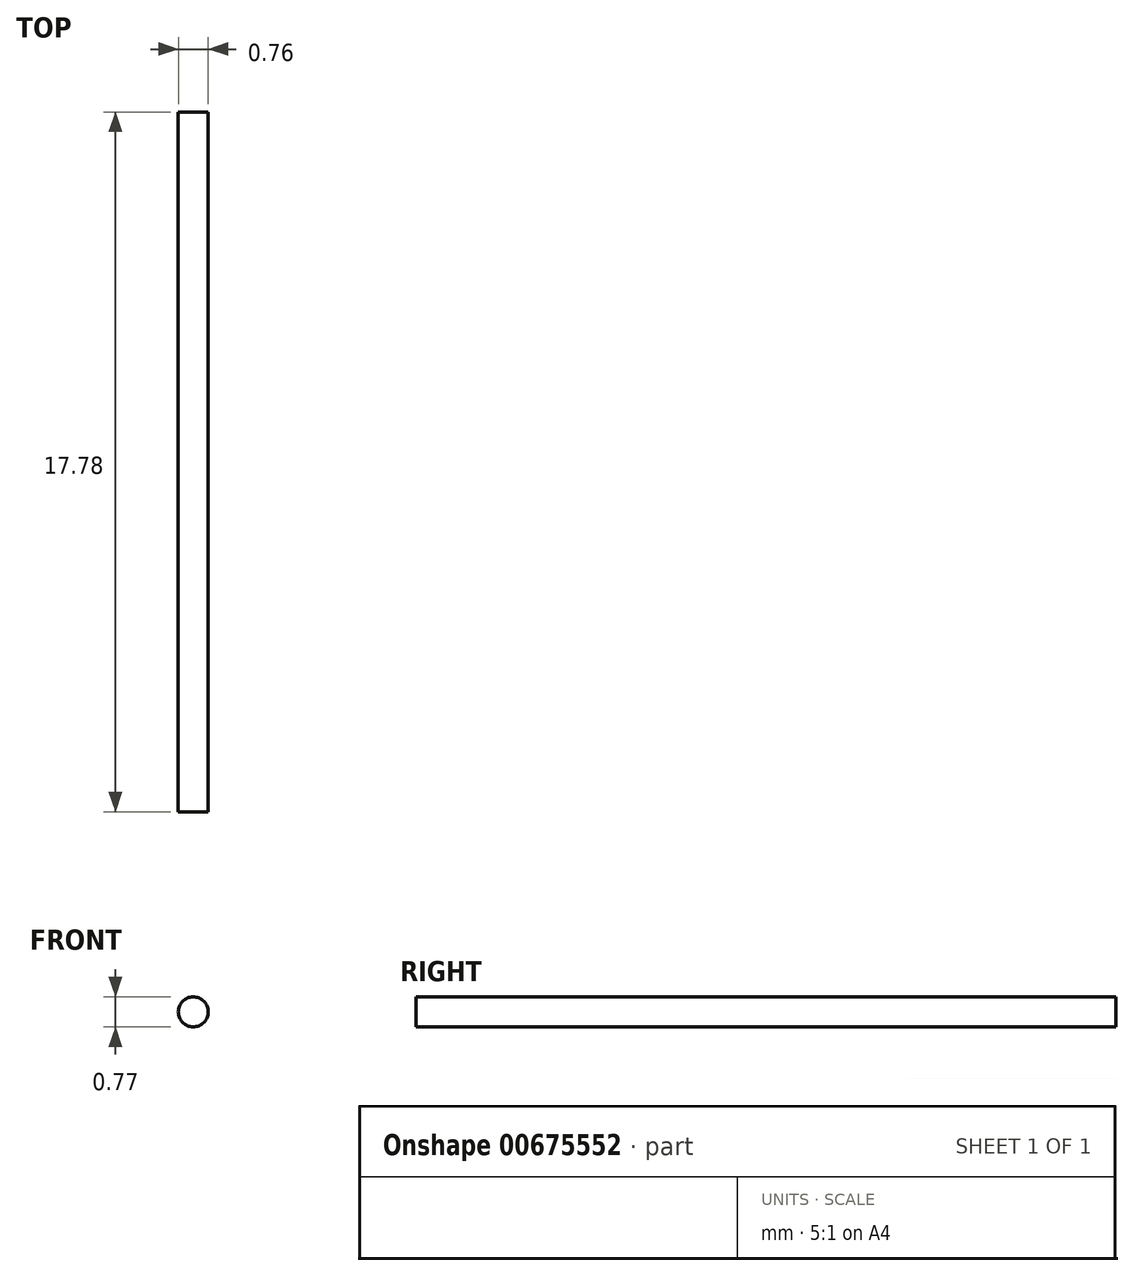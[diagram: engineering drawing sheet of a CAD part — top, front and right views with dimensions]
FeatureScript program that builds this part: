
annotation { "Feature Type Name" : "Feature", "Feature Type Description" : "" }
export const myFeature = defineFeature(function(context is Context, id is Id, definition is map)
    precondition{}
    {
        {
            var Q0;
            Q0=qCreatedBy(makeId("Front.planeOp"),FACE);
            var sketch = newSketch(context, id + "F0", { "sketchPlane" : qUnion([Q0])});
            skCircle(sketch, "E0", {"center": v(-44.96, 25.03) * mm, "radius": 0.38 * mm});
            skSolve(sketch);
        }
        {
            var Q0;
            Q0 = qSketchRegion(id + "F0", true);
            extrude(context, id + "F1", {"entities" : qUnion([Q0]), "depth" : 17.78 * mm, "offsetDistance" : 25.4 * mm});
        }
    });
